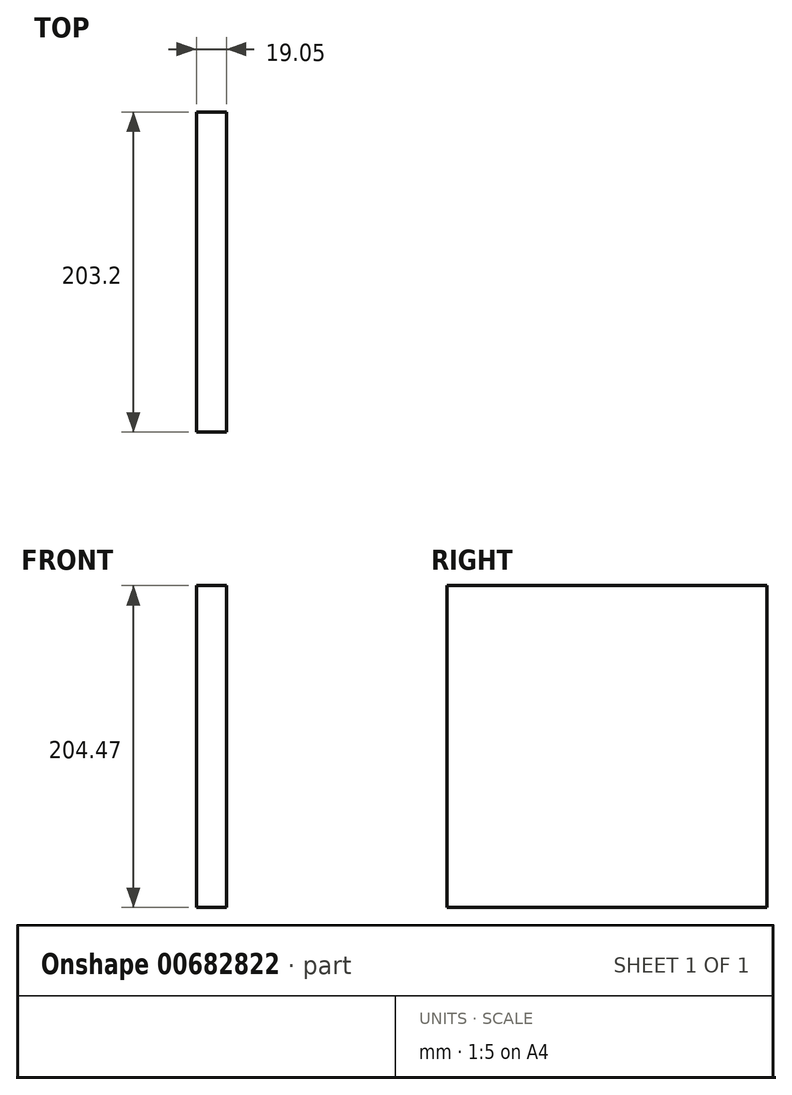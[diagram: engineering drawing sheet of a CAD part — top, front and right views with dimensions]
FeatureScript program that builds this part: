
annotation { "Feature Type Name" : "Feature", "Feature Type Description" : "" }
export const myFeature = defineFeature(function(context is Context, id is Id, definition is map)
    precondition{}
    {
        {
            var Q0;
            Q0=qCreatedBy(makeId("Right.planeOp"),FACE);
            var sketch = newSketch(context, id + "F0", { "sketchPlane" : qUnion([Q0])});
            skLineSegment(sketch, "E0.bottom", {"start": v(0, 0) * mm, "end": v(-203.2, 0) * mm});
            skLineSegment(sketch, "E0.top", {"start": v(0, 204.47) * mm, "end": v(-203.2, 204.47) * mm});
            skLineSegment(sketch, "E0.left", {"start": v(0, 0) * mm, "end": v(0, 204.47) * mm});
            skLineSegment(sketch, "E0.right", {"start": v(-203.2, 0) * mm, "end": v(-203.2, 204.47) * mm});
            skSolve(sketch);
        }
        {
            var Q0;
            Q0=qSketchRegion(id+"F0",true);
            extrude(context, id + "F1", {"entities" : qUnion([Q0]), "depth" : 19.05 * mm, "offsetDistance" : 25.4 * mm});
        }
    });
